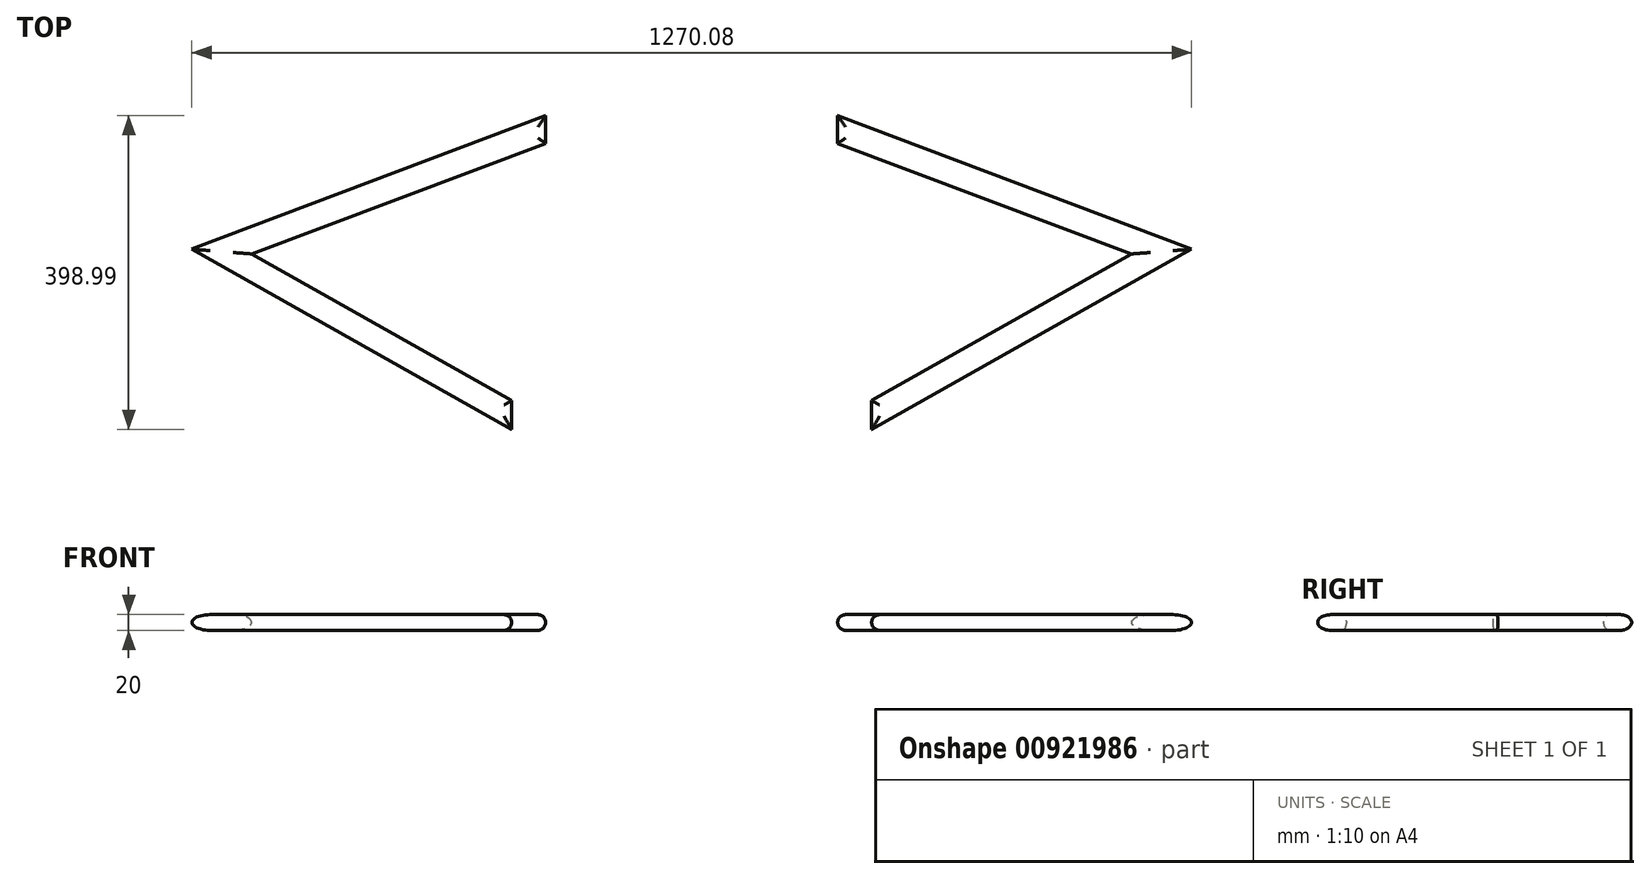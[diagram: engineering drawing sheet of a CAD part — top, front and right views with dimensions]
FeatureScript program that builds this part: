
annotation { "Feature Type Name" : "Feature", "Feature Type Description" : "" }
export const myFeature = defineFeature(function(context is Context, id is Id, definition is map)
    precondition{}
    {
        {
            var Q0;
            Q0=qCreatedBy(makeId("Top.planeOp"),FACE);
            var sketch = newSketch(context, id + "F0", { "sketchPlane" : qUnion([Q0])});
            skLineSegment(sketch, "E0", {"start": v(185.4, 1852.26) * mm, "end": v(635.04, 1682.48) * mm});
            skLineSegment(sketch, "E1", {"start": v(635.04, 1682.48) * mm, "end": v(228.54, 1453.27) * mm});
            skLineSegment(sketch, "E2", {"start": v(228.54, 1453.27) * mm, "end": v(228.54, 1490.24) * mm});
            skLineSegment(sketch, "E3", {"start": v(228.54, 1490.24) * mm, "end": v(558.82, 1676.47) * mm});
            skLineSegment(sketch, "E4", {"start": v(558.82, 1676.47) * mm, "end": v(185.4, 1816.8) * mm});
            skLineSegment(sketch, "E5", {"start": v(185.4, 1816.8) * mm, "end": v(185.4, 1852.26) * mm});
            skSolve(sketch);
        }
        {
            var Q0;
            Q0=makeQuery(id+"F0.imprint","IMPRINT",FACE,{"disambiguationData":[TD([[makeQuery(id+"F0.imprint","IMPRINT",EDGE,{"derivedFrom":sQuery(id+"F0.wireOp",EDGE,"E0")}),-1.0]])]});
            extrude(context, id + "F1", {"entities" : qUnion([Q0]), "depth" : 20 * mm, "offsetDistance" : 25 * mm});
        }
        {
            var Q0;
            Q0=makeQuery(id+"F1.opExtrude","CAP_FACE",FACE,{"disambiguationData":[OSD([sQuery(id+"F0.wireOp",EDGE,"E0"),sQuery(id+"F0.wireOp",EDGE,"E1"),sQuery(id+"F0.wireOp",EDGE,"E2"),sQuery(id+"F0.wireOp",EDGE,"E3"),sQuery(id+"F0.wireOp",EDGE,"E4"),sQuery(id+"F0.wireOp",EDGE,"E5")])],"isStart":false});
            var Q1;
            Q1=makeQuery(id+"F1.opExtrude","CAP_FACE",FACE,{"disambiguationData":[OSD([sQuery(id+"F0.wireOp",EDGE,"E0"),sQuery(id+"F0.wireOp",EDGE,"E1"),sQuery(id+"F0.wireOp",EDGE,"E2"),sQuery(id+"F0.wireOp",EDGE,"E3"),sQuery(id+"F0.wireOp",EDGE,"E4"),sQuery(id+"F0.wireOp",EDGE,"E5")])],"isStart":true});
            fillet(context, id + "F2", {"entities" : qUnion([Q0, Q1]), "radius" : 10 * mm, "tangentPropagation" : true, "allowEdgeOverflow" : false});
        }
        {
            var Q0;
            Q0=makeQuery(id+"F1.opExtrude","SWEPT_BODY",BODY,{"disambiguationData":[OSD([sQuery(id+"F0.wireOp",EDGE,"E0"),sQuery(id+"F0.wireOp",EDGE,"E1"),sQuery(id+"F0.wireOp",EDGE,"E2"),sQuery(id+"F0.wireOp",EDGE,"E3"),sQuery(id+"F0.wireOp",EDGE,"E4"),sQuery(id+"F0.wireOp",EDGE,"E5")])]});
            var Q1;
            Q1=qCreatedBy(makeId("Right.planeOp"),FACE);
            mirror(context, id + "F3", {"entities" : qUnion([Q0]), "mirrorPlane" : qUnion([Q1])});
        }
    });
